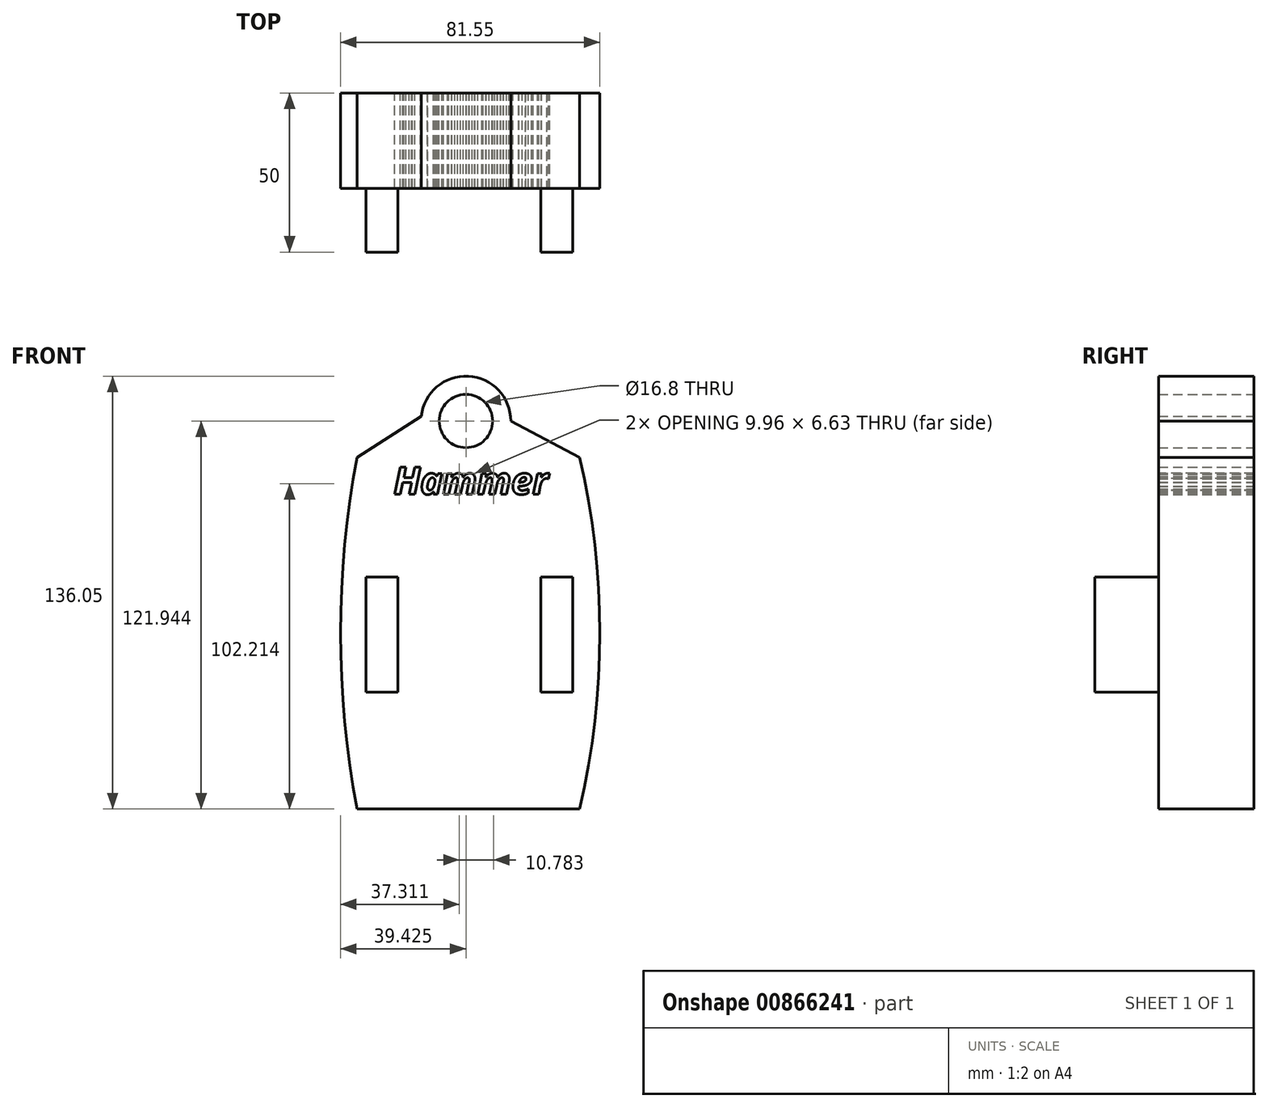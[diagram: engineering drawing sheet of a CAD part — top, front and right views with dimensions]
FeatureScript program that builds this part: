
annotation { "Feature Type Name" : "Feature", "Feature Type Description" : "" }
export const myFeature = defineFeature(function(context is Context, id is Id, definition is map)
    precondition{}
    {
        {
            var Q0;
            Q0=qCreatedBy(makeId("Front.planeOp"),FACE);
            var sketch = newSketch(context, id + "F0", { "sketchPlane" : qUnion([Q0])});
            skLineSegment(sketch, "E0.top", {"start": v(-23.43, -69.86) * mm, "end": v(46.57, -69.86) * mm});
            skArc(sketch, "E1", {"start": v(24.94, 52.08) * mm, "mid": v(11.57, 66.17) * mm, "end": v(-3.2, 53.56) * mm});
            skCircle(sketch, "E2", {"center": v(10.84, 52.08) * mm, "radius": 8.4 * mm});
            skLineSegment(sketch, "E3", {"start": v(-23.43, 40.66) * mm, "end": v(-3.2, 53.56) * mm});
            skLineSegment(sketch, "E4", {"start": v(24.94, 52.08) * mm, "end": v(46.57, 40.66) * mm});
            skArc(sketch, "E5", {"start": v(-23.43, 40.66) * mm, "mid": v(-28.59, -14.6) * mm, "end": v(-23.43, -69.86) * mm});
            skArc(sketch, "E6", {"start": v(46.57, -69.86) * mm, "mid": v(52.96, -14.6) * mm, "end": v(46.57, 40.66) * mm});
            skSolve(sketch);
        }
        {
            var Q0;
            Q0 = qSketchRegion(id + "F0", true);
            extrude(context, id + "F1", {"entities" : qUnion([Q0]), "depth" : 30 * mm, "offsetDistance" : 25 * mm});
        }
        {
            var Q0;
            Q0=qCreatedBy(makeId("Front.planeOp"),FACE);
            var sketch = newSketch(context, id + "F2", { "sketchPlane" : qUnion([Q0])});
            skLineSegment(sketch, "E7.bottom", {"start": v(-20.59, 3.07) * mm, "end": v(-10.59, 3.07) * mm});
            skLineSegment(sketch, "E7.top", {"start": v(-20.59, -33.12) * mm, "end": v(-10.59, -33.12) * mm});
            skLineSegment(sketch, "E7.left", {"start": v(-20.59, 3.07) * mm, "end": v(-20.59, -33.12) * mm});
            skLineSegment(sketch, "E7.right", {"start": v(-10.59, 3.07) * mm, "end": v(-10.59, -33.12) * mm});
            skLineSegment(sketch, "E8.bottom", {"start": v(34.41, 3.07) * mm, "end": v(44.41, 3.07) * mm});
            skLineSegment(sketch, "E8.top", {"start": v(34.41, -33.12) * mm, "end": v(44.41, -33.12) * mm});
            skLineSegment(sketch, "E8.left", {"start": v(34.41, 3.07) * mm, "end": v(34.41, -33.12) * mm});
            skLineSegment(sketch, "E8.right", {"start": v(44.41, 3.07) * mm, "end": v(44.41, -33.12) * mm});
            skSolve(sketch);
        }
        {
            var Q0;
            Q0 = qSketchRegion(id + "F2", true);
            extrude(context, id + "F3", {"entities" : qUnion([Q0]), "operationType" : NewBodyOperationType.ADD, "depth" : 50 * mm, "offsetDistance" : 25 * mm});
        }
        {
            var Q0;
            Q0=qCreatedBy(makeId("Front.planeOp"),FACE);
            var sketch = newSketch(context, id + "F4", { "sketchPlane" : qUnion([Q0])});
            skText(sketch, "E9", { "text": "Hammer", "fontName": "OpenSans-BoldItalic.ttf"});
            const initialGuessF4  = {"E9": [-0.0119, 0.02904, 1, 0, 0.00858]};
            skSetInitialGuess(sketch, initialGuessF4);
            skSolve(sketch);
        }
        {
            var Q0;
            Q0 = qSketchRegion(id + "F4", true);
            extrude(context, id + "F5", {"entities" : qUnion([Q0]), "operationType" : NewBodyOperationType.REMOVE, "depth" : 50 * mm, "offsetDistance" : 25 * mm});
        }
    });
